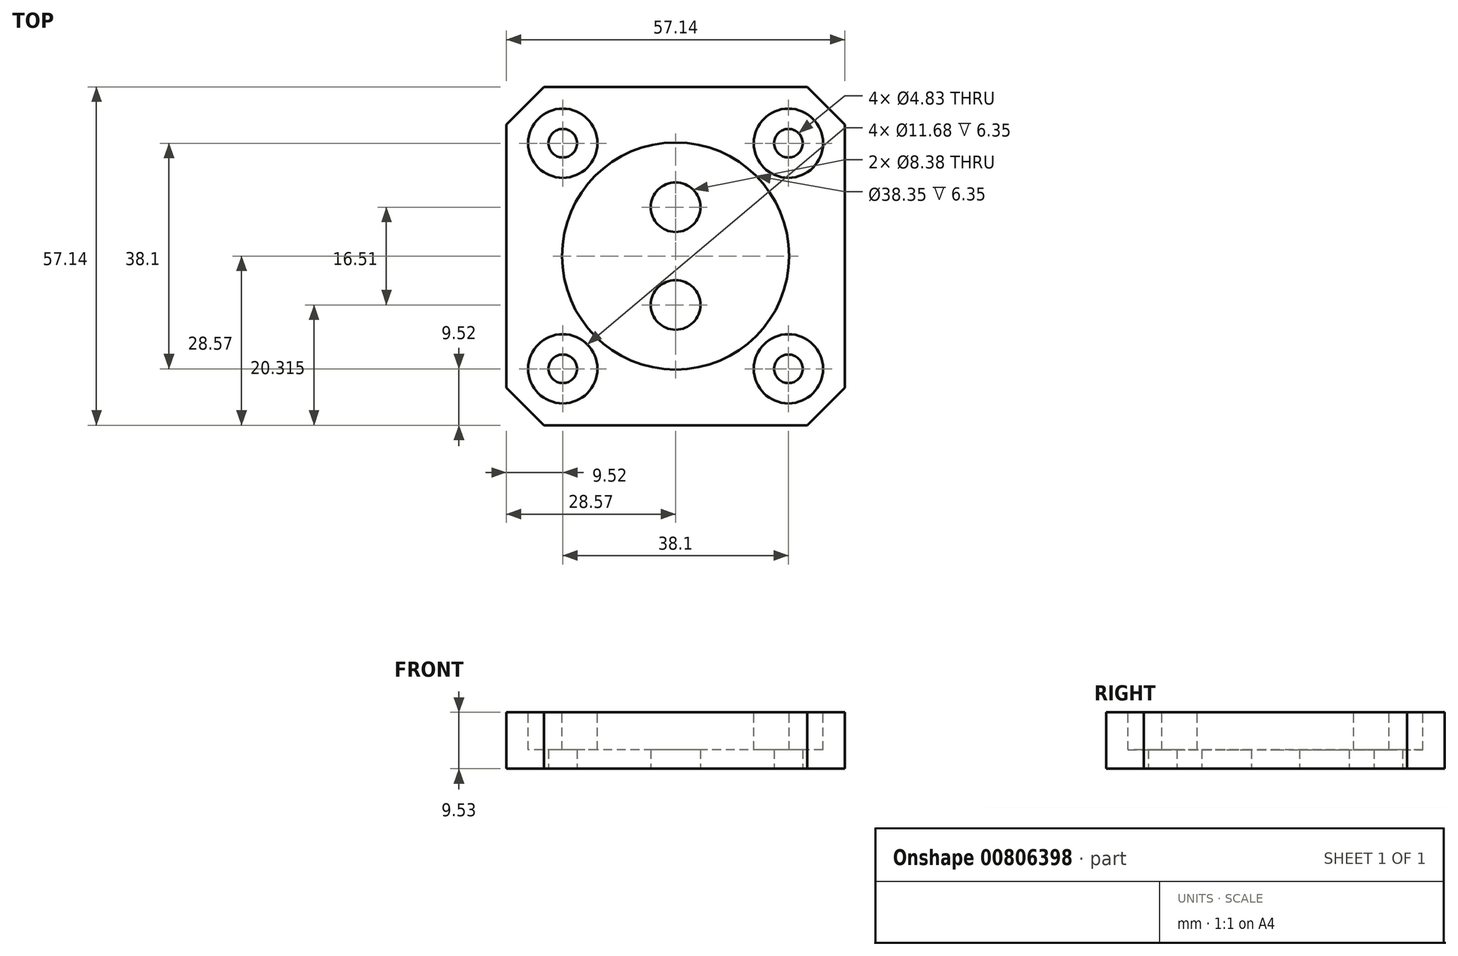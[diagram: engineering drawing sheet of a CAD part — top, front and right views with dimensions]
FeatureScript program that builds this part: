
annotation { "Feature Type Name" : "Feature", "Feature Type Description" : "" }
export const myFeature = defineFeature(function(context is Context, id is Id, definition is map)
    precondition{}
    {
        {
            var Q0;
            Q0=qCreatedBy(makeId("Top.planeOp"),FACE);
            var sketch = newSketch(context, id + "F0", { "sketchPlane" : qUnion([Q0])});
            skLineSegment(sketch, "E0.bottom", {"start": v(-28.58, 28.58) * mm, "end": v(28.58, 28.57) * mm});
            skLineSegment(sketch, "E0.top", {"start": v(-28.58, -28.57) * mm, "end": v(28.58, -28.58) * mm});
            skLineSegment(sketch, "E0.left", {"start": v(-28.57, 28.57) * mm, "end": v(-28.58, -28.57) * mm});
            skLineSegment(sketch, "E0.right", {"start": v(28.58, 28.57) * mm, "end": v(28.57, -28.57) * mm});
            skSolve(sketch);
        }
        {
            var Q0;
            Q0 = qSketchRegion(id + "F0", true);
            extrude(context, id + "F1", {"entities" : qUnion([Q0]), "depth" : 9.52 * mm, "offsetDistance" : 25.4 * mm});
        }
        {
            var Q0;
            Q0=makeQuery(id+"F1.opExtrude","CAP_FACE",FACE,{"disambiguationData":[OSD([sQuery(id+"F0.wireOp",EDGE,"E0.bottom"),sQuery(id+"F0.wireOp",EDGE,"E0.top"),sQuery(id+"F0.wireOp",EDGE,"E0.left"),sQuery(id+"F0.wireOp",EDGE,"E0.right")])],"isStart":false});
            var sketch = newSketch(context, id + "F2", { "sketchPlane" : qUnion([Q0])});
            skCircle(sketch, "E1", {"center": v(0, 0) * mm, "radius": 19.18 * mm});
            skSolve(sketch);
        }
        {
            var Q0;
            Q0 = qSketchRegion(id + "F2", true);
            extrude(context, id + "F3", {"entities" : qUnion([Q0]), "operationType" : NewBodyOperationType.REMOVE, "oppositeDirection" : true, "depth" : 6.35 * mm, "offsetDistance" : 25.4 * mm});
        }
        {
            var Q0;
            Q0=qCreatedBy(makeId("Top.planeOp"),FACE);
            var sketch = newSketch(context, id + "F4", { "sketchPlane" : qUnion([Q0])});
            skCircle(sketch, "E2", {"center": v(-19.05, 19.05) * mm, "radius": 2.41 * mm});
            skCircle(sketch, "E3", {"center": v(19.05, 19.05) * mm, "radius": 2.41 * mm});
            skCircle(sketch, "E4", {"center": v(-19.05, -19.05) * mm, "radius": 2.41 * mm});
            skCircle(sketch, "E5", {"center": v(19.05, -19.05) * mm, "radius": 2.41 * mm});
            skSolve(sketch);
        }
        {
            var Q0;
            Q0 = qSketchRegion(id + "F4", true);
            extrude(context, id + "F5", {"entities" : qUnion([Q0]), "operationType" : NewBodyOperationType.REMOVE, "endBound" : BoundingType.THROUGH_ALL, "depth" : 25.4 * mm, "offsetDistance" : 25.4 * mm});
        }
        {
            var Q0;
            Q0=makeQuery(id+"F1.opExtrude","CAP_FACE",FACE,{"disambiguationData":[OSD([sQuery(id+"F0.wireOp",EDGE,"E0.bottom"),sQuery(id+"F0.wireOp",EDGE,"E0.top"),sQuery(id+"F0.wireOp",EDGE,"E0.left"),sQuery(id+"F0.wireOp",EDGE,"E0.right")])],"isStart":false});
            var sketch = newSketch(context, id + "F6", { "sketchPlane" : qUnion([Q0])});
            skCircle(sketch, "E6.0", {"center": v(-19.05, 19.05) * mm, "radius": 2.41 * mm, "construction": true});
            skCircle(sketch, "E7.0", {"center": v(19.05, 19.05) * mm, "radius": 2.41 * mm, "construction": true});
            skCircle(sketch, "E8.0", {"center": v(19.05, -19.05) * mm, "radius": 2.41 * mm, "construction": true});
            skCircle(sketch, "E9.0", {"center": v(-19.05, -19.05) * mm, "radius": 2.41 * mm, "construction": true});
            skCircle(sketch, "E10", {"center": v(-19.05, 19.05) * mm, "radius": 5.84 * mm});
            skCircle(sketch, "E11", {"center": v(19.05, 19.05) * mm, "radius": 5.84 * mm});
            skCircle(sketch, "E12", {"center": v(-19.05, -19.05) * mm, "radius": 5.84 * mm});
            skCircle(sketch, "E13", {"center": v(19.05, -19.05) * mm, "radius": 5.84 * mm});
            skSolve(sketch);
        }
        {
            var Q0;
            Q0=qCreatedBy(makeId("Top.planeOp"),FACE);
            var sketch = newSketch(context, id + "F7", { "sketchPlane" : qUnion([Q0])});
            skCircle(sketch, "E14", {"center": v(0, 8.26) * mm, "radius": 4.2 * mm});
            skCircle(sketch, "E15", {"center": v(0, -8.26) * mm, "radius": 4.2 * mm});
            skSolve(sketch);
        }
        {
            var Q0;
            Q0 = qSketchRegion(id + "F7", true);
            extrude(context, id + "F8", {"entities" : qUnion([Q0]), "operationType" : NewBodyOperationType.REMOVE, "endBound" : BoundingType.THROUGH_ALL, "depth" : 25.4 * mm, "offsetDistance" : 25.4 * mm});
        }
        {
            var Q0;
            Q0 = qSketchRegion(id + "F6", true);
            extrude(context, id + "F9", {"entities" : qUnion([Q0]), "operationType" : NewBodyOperationType.REMOVE, "oppositeDirection" : true, "depth" : 6.35 * mm, "offsetDistance" : 25.4 * mm});
        }
        {
            var Q0;
            Q0=makeQuery(id+"F1.opExtrude","SWEPT_EDGE",EDGE,{"disambiguationData":[OSD([sQuery(id+"F0.wireOp",EDGE,"E0.top"),sQuery(id+"F0.wireOp",EDGE,"E0.left")])]});
            var Q1;
            Q1=makeQuery(id+"F1.opExtrude","SWEPT_EDGE",EDGE,{"disambiguationData":[OSD([sQuery(id+"F0.wireOp",EDGE,"E0.top"),sQuery(id+"F0.wireOp",EDGE,"E0.right")])]});
            var Q2;
            Q2=makeQuery(id+"F1.opExtrude","SWEPT_EDGE",EDGE,{"disambiguationData":[OSD([sQuery(id+"F0.wireOp",EDGE,"E0.bottom"),sQuery(id+"F0.wireOp",EDGE,"E0.right")])]});
            var Q3;
            Q3=makeQuery(id+"F1.opExtrude","SWEPT_EDGE",EDGE,{"disambiguationData":[OSD([sQuery(id+"F0.wireOp",EDGE,"E0.bottom"),sQuery(id+"F0.wireOp",EDGE,"E0.left")])]});
            chamfer(context, id + "F10", {"entities" : qUnion([Q0, Q1, Q2, Q3]), "width" : 6.35 * mm, "tangentPropagation" : true});
        }
    });
